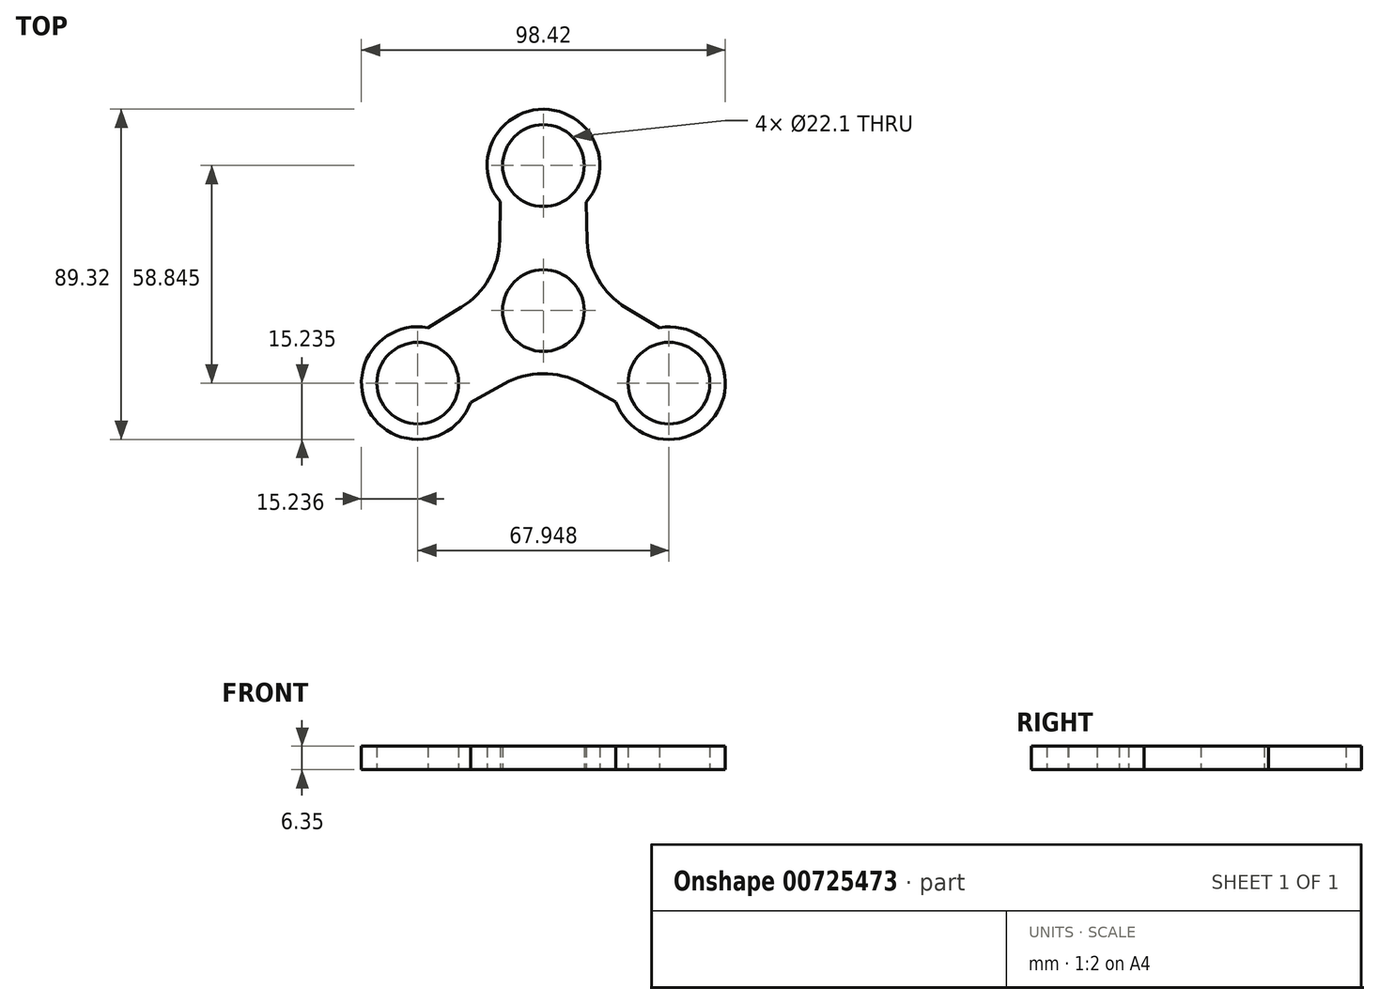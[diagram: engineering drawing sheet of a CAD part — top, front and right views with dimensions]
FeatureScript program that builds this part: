
annotation { "Feature Type Name" : "Feature", "Feature Type Description" : "" }
export const myFeature = defineFeature(function(context is Context, id is Id, definition is map)
    precondition{}
    {
        {
            var Q0;
            Q0=qCreatedBy(makeId("Top.planeOp"),FACE);
            var sketch = newSketch(context, id + "F0", { "sketchPlane" : qUnion([Q0])});
            skCircle(sketch, "E0", {"center": v(0, 0) * mm, "radius": 11.05 * mm});
            skCircle(sketch, "E1", {"center": v(0, 0) * mm, "radius": 13.97 * mm});
            skCircle(sketch, "E2", {"center": v(0, 39.23) * mm, "radius": 11.05 * mm});
            skCircle(sketch, "E3", {"center": v(0, 39.23) * mm, "radius": 15.24 * mm});
            skCircle(sketch, "E4.1.0", {"center": v(-33.97, -19.61) * mm, "radius": 11.05 * mm});
            skCircle(sketch, "E4.2.0", {"center": v(33.97, -19.61) * mm, "radius": 11.05 * mm});
            skCircle(sketch, "E5.1.0", {"center": v(-33.97, -19.61) * mm, "radius": 15.24 * mm});
            skCircle(sketch, "E5.2.0", {"center": v(33.97, -19.61) * mm, "radius": 15.24 * mm});
            skPoint(sketch, "E6", {"position": v(-11.72, 29.48) * mm});
            skPoint(sketch, "E7", {"position": v(-12, 7.15) * mm});
            skPoint(sketch, "E8", {"position": v(-31.22, -4.62) * mm});
            skLineSegment(sketch, "E9", {"start": v(-11.72, 29.48) * mm, "end": v(-11.85, 19.06) * mm});
            skLineSegment(sketch, "E10", {"start": v(-31.22, -4.62) * mm, "end": v(-22.16, 0.92) * mm});
            skArc(sketch, "E11.filletArc", {"start": v(-22.16, 0.92) * mm, "mid": v(-14.67, 8.66) * mm, "end": v(-11.85, 19.06) * mm});
            skArc(sketch, "E12.1.0", {"start": v(10.28, -19.66) * mm, "mid": v(-0.17, -17.04) * mm, "end": v(-10.58, -19.8) * mm});
            skArc(sketch, "E12.2.0", {"start": v(11.88, 18.73) * mm, "mid": v(14.84, 8.37) * mm, "end": v(22.43, 0.73) * mm});
            skLineSegment(sketch, "E13.1.0", {"start": v(-19.68, -24.89) * mm, "end": v(-10.58, -19.8) * mm});
            skLineSegment(sketch, "E13.2.0", {"start": v(31.4, -4.6) * mm, "end": v(22.43, 0.73) * mm});
            skLineSegment(sketch, "E14.1.0", {"start": v(19.62, -24.73) * mm, "end": v(10.28, -19.66) * mm});
            skLineSegment(sketch, "E14.2.0", {"start": v(11.6, 29.35) * mm, "end": v(11.88, 18.73) * mm});
            skSolve(sketch);
        }
        {
            var Q0;
            Q0 = qSketchRegion(id + "F0", true);
            var Q1;
            Q1=makeQuery(id+"F0.imprint","IMPRINT",FACE,{"disambiguationData":[TD([[makeQuery(id+"F0.imprint","IMPRINT",EDGE,{"derivedFrom":sQuery(id+"F0.wireOp",EDGE,"E0")}),-1.0]])]});
            extrude(context, id + "F1", {"entities" : qUnion([Q0, Q1]), "depth" : 6.35 * mm, "offsetDistance" : 25.4 * mm});
        }
    });
